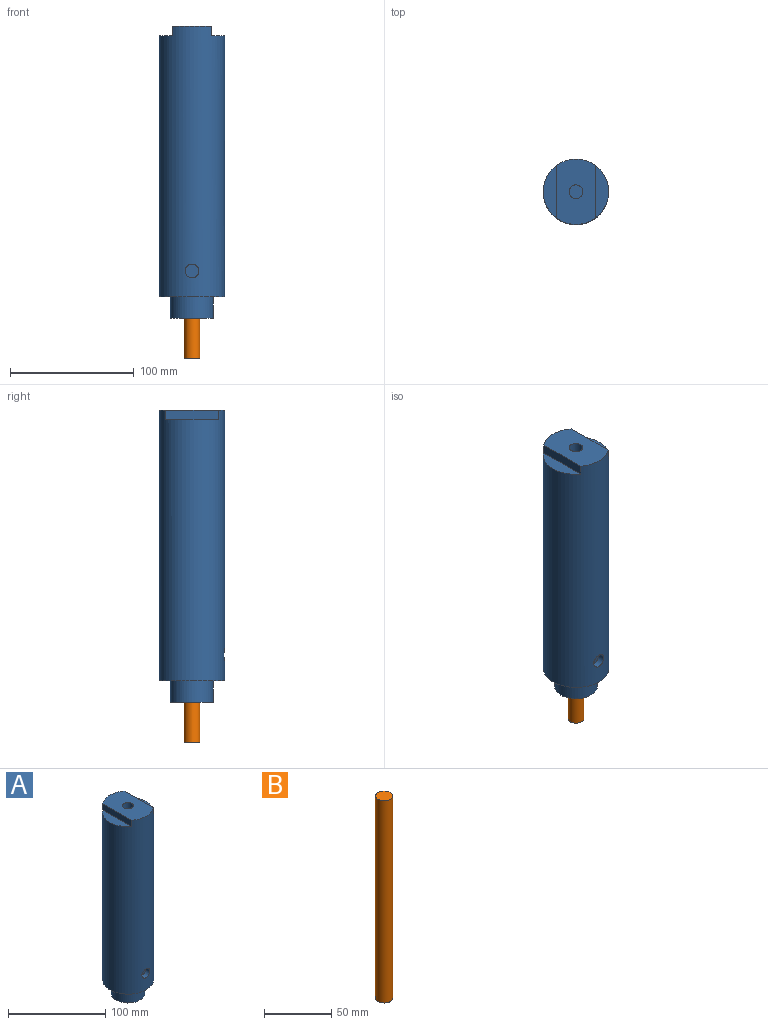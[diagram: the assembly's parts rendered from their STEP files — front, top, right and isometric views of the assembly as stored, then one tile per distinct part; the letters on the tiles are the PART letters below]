
ASSEMBLY  parts=2 mates=1
PART A: 15 faces, bbox 52.8x52.8x236.5 mm
  f0: plane 42.23x10.54mm, normal (0,0,1), area 311.1mm2, adj f1,f5
  f1: cylinder r=26.42mm len=218.95mm, axis (0,0,-1), area 35471.2mm2, adj f0,f2,f3,f4,f5,f6,f13
  f2: plane 42.23x10.54mm, normal (0,0,1), area 311.1mm2, adj f1,f4
  f3: plane 52.83x52.83mm, normal (0,0,-1), area 1241.2mm2, adj f1,f9
  f4: plane 42.23x7.87mm, normal (-1,0,0), area 332.5mm2, adj f1,f2,f6
  f5: plane 42.23x7.87mm, normal (1,0,0), area 332.5mm2, adj f0,f1,f6
  f6: plane 52.83x31.75mm, normal (0,0,1), area 1472.9mm2, adj f1,f4,f5,f7
  f7: cylinder r=5.56mm len=12.7mm, axis (0,0,1), area 443.9mm2, adj f6,f8
  f8: plane 11.13x11.13mm, normal (0,0,1), area 97.2mm2, adj f7
  f9: cylinder r=17.4mm len=34.8mm, axis (0,0,1), area 1916mm2, adj f3,f10
  f10: plane 34.8x34.8mm, normal (0,0,-1), area 824.4mm2, adj f9,f11
  f11: cylinder r=6.35mm len=152.4mm, axis (0,0,-1), area 6080.5mm2, adj f10,f12
  f12: plane 12.7x12.7mm, normal (0,0,-1), area 126.7mm2, adj f11
  f13: cylinder r=5.56mm len=11.13mm, axis (0,-1,0), area 202.8mm2, adj f1,f14
  f14: plane 11.13x11.13mm, normal (0,-1,0), area 97.2mm2, adj f13
PART B: 3 faces, bbox 12.7x12.7x184.4 mm
  f0: cylinder r=6.35mm len=184.4mm, axis (0,0,-1), area 7357.4mm2, adj f1,f2
  f1: plane 12.7x12.7mm, normal (0,0,1), area 126.7mm2, adj f0
  f2: plane 12.7x12.7mm, normal (0,0,-1), area 126.7mm2, adj f0
PLACE A t=(-0.86,-0.31,5.1)mm fixed
PLACE B t=(-0.86,-0.31,-57.77)mm
MATE slider B.f0 <-> A.f9  axis (0,0,1) through (-0.86,-0.31,34.44)mm
